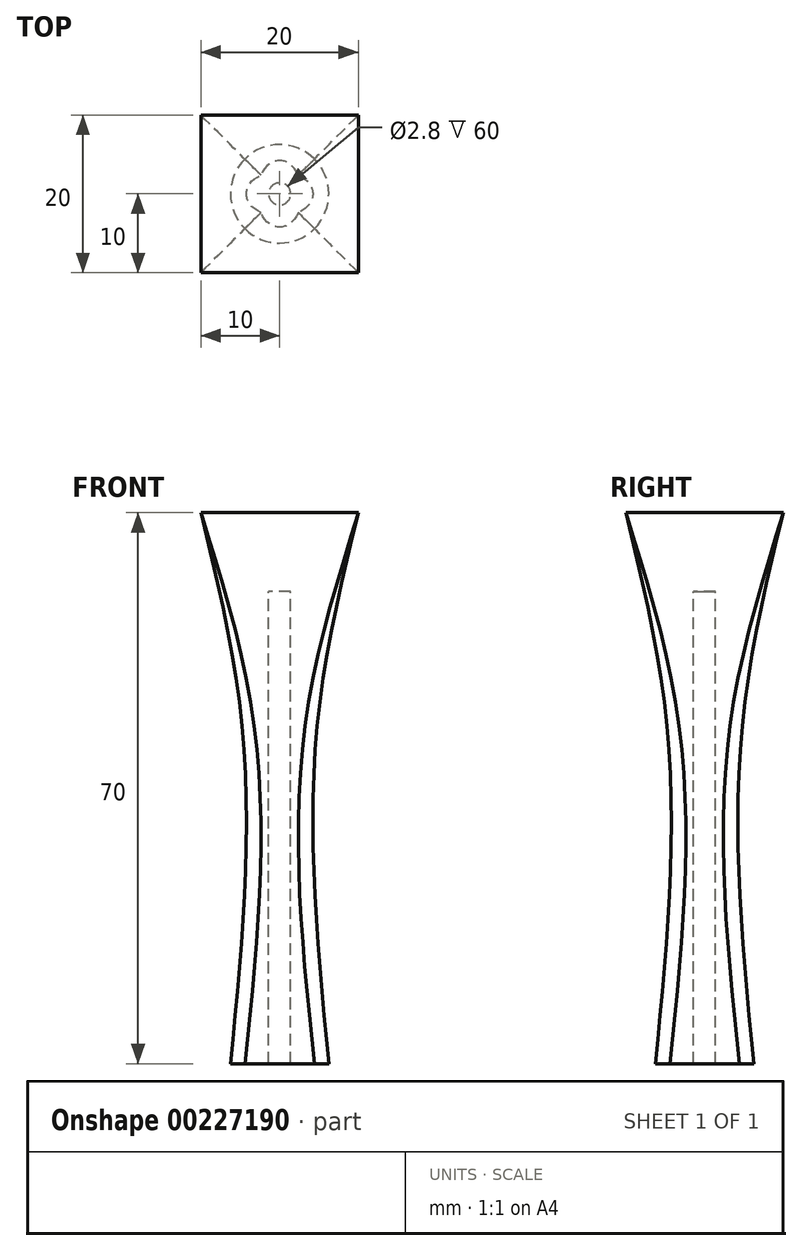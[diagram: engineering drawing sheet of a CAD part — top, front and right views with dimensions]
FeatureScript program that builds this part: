
annotation { "Feature Type Name" : "Feature", "Feature Type Description" : "" }
export const myFeature = defineFeature(function(context is Context, id is Id, definition is map)
    precondition{}
    {
        {
            var Q0;
            Q0=qCreatedBy(makeId("Top.planeOp"),FACE);
            var sketch = newSketch(context, id + "F0", { "sketchPlane" : qUnion([Q0])});
            skLineSegment(sketch, "E0", {"start": v(0, 0) * mm, "end": v(0, 6.25) * mm, "construction": true});
            skArc(sketch, "E1", {"start": v(-4.42, 4.42) * mm, "mid": v(-6.25, 0) * mm, "end": v(-4.42, -4.42) * mm});
            skArc(sketch, "E2", {"start": v(-4.42, -4.42) * mm, "mid": v(0, -6.25) * mm, "end": v(4.42, -4.42) * mm});
            skArc(sketch, "E3", {"start": v(4.42, -4.42) * mm, "mid": v(6.25, 0) * mm, "end": v(4.42, 4.42) * mm});
            skArc(sketch, "E4", {"start": v(4.42, 4.42) * mm, "mid": v(0, 6.25) * mm, "end": v(-4.42, 4.42) * mm});
            skLineSegment(sketch, "E5", {"start": v(-4.42, 4.42) * mm, "end": v(0, 0) * mm, "construction": true});
            skLineSegment(sketch, "E6", {"start": v(0, 0) * mm, "end": v(-4.42, -4.42) * mm, "construction": true});
            skLineSegment(sketch, "E7", {"start": v(0, 0) * mm, "end": v(4.42, -4.42) * mm, "construction": true});
            skLineSegment(sketch, "E8", {"start": v(4.42, 4.42) * mm, "end": v(0, 0) * mm, "construction": true});
            skSolve(sketch);
        }
        {
            var Q0;
            Q0=qCreatedBy(makeId("Top.planeOp"),FACE);
            cPlane(context, id + "F1", {"entities" : qUnion([Q0]), "cplaneType" : CPlaneType.OFFSET, "offset" : 45 * mm, "width" : 150 * mm, "height" : 150 * mm});
        }
        {
            var Q0;
            Q0=qCreatedBy(id+"F1.planeOp",FACE);
            var sketch = newSketch(context, id + "F2", { "sketchPlane" : qUnion([Q0])});
            skCircle(sketch, "E9", {"center": v(0, 0) * mm, "radius": 5 * mm});
            skLineSegment(sketch, "E10", {"start": v(0, 0) * mm, "end": v(0, 5) * mm, "construction": true});
            skLineSegment(sketch, "E11.0", {"start": v(-4.42, 4.42) * mm, "end": v(-3.54, 3.54) * mm, "construction": true});
            skLineSegment(sketch, "E12.0", {"start": v(0, 0) * mm, "end": v(-3.54, -3.54) * mm, "construction": true});
            skLineSegment(sketch, "E13.0", {"start": v(0, 0) * mm, "end": v(3.54, -3.54) * mm, "construction": true});
            skLineSegment(sketch, "E14.0", {"start": v(4.42, 4.42) * mm, "end": v(3.54, 3.54) * mm, "construction": true});
            skLineSegment(sketch, "E15", {"start": v(-3.54, 3.54) * mm, "end": v(0, 0) * mm, "construction": true});
            skLineSegment(sketch, "E16", {"start": v(-3.54, -3.54) * mm, "end": v(-4.42, -4.42) * mm, "construction": true});
            skLineSegment(sketch, "E17", {"start": v(3.54, -3.54) * mm, "end": v(4.42, -4.42) * mm, "construction": true});
            skLineSegment(sketch, "E18", {"start": v(3.54, 3.54) * mm, "end": v(0, 0) * mm, "construction": true});
            skSolve(sketch);
        }
        {
            var Q0;
            Q0=qCreatedBy(id+"F1.planeOp",FACE);
            cPlane(context, id + "F3", {"entities" : qUnion([Q0]), "cplaneType" : CPlaneType.OFFSET, "offset" : 25 * mm, "width" : 150 * mm, "height" : 150 * mm});
        }
        {
            var Q0;
            Q0=qCreatedBy(id+"F3.planeOp",FACE);
            var sketch = newSketch(context, id + "F4", { "sketchPlane" : qUnion([Q0])});
            skLineSegment(sketch, "E19.bottom", {"start": v(-10, 10) * mm, "end": v(10, 10) * mm});
            skLineSegment(sketch, "E19.top", {"start": v(-10, -10) * mm, "end": v(10, -10) * mm});
            skLineSegment(sketch, "E19.left", {"start": v(-10, 10) * mm, "end": v(-10, -10) * mm});
            skLineSegment(sketch, "E19.right", {"start": v(10, 10) * mm, "end": v(10, -10) * mm});
            skPoint(sketch, "E19.middle", {"position": v(0, 0) * mm});
            skSolve(sketch);
        }
        {
            var Q0;
            Q0=makeQuery(id+"F0.imprint","IMPRINT",FACE,{"disambiguationData":[TD([[makeQuery(id+"F0.imprint","IMPRINT",EDGE,{"derivedFrom":sQuery(id+"F0.wireOp",EDGE,"E1")}),1.0]])]});
            var Q1;
            Q1=makeQuery(id+"F2.imprint","IMPRINT",FACE,{"disambiguationData":[TD([[makeQuery(id+"F2.imprint","IMPRINT",EDGE,{"derivedFrom":sQuery(id+"F2.wireOp",EDGE,"E9")}),1.0]])]});
            var Q2;
            Q2=makeQuery(id+"F4.imprint","IMPRINT",FACE,{"disambiguationData":[TD([[makeQuery(id+"F4.imprint","IMPRINT",EDGE,{"derivedFrom":sQuery(id+"F4.wireOp",EDGE,"E19.bottom")}),-1.0]])]});
            loft(context, id + "F5", {"sheetProfilesArray" : [{ "sheetProfileEntities" : qUnion([Q0]) }, { "sheetProfileEntities" : qUnion([Q1]) }, { "sheetProfileEntities" : qUnion([Q2]) }]});
        }
        {
            var Q0;
            Q0=makeQuery(id+"F5.opLoft","CAP_FACE",FACE,{"disambiguationData":[OSD([makeQuery(id+"F4.imprint","IMPRINT",FACE,{"disambiguationData":[TD([[makeQuery(id+"F4.imprint","IMPRINT",EDGE,{"derivedFrom":sQuery(id+"F4.wireOp",EDGE,"E19.bottom")}),-1.0]])]})])],"isStart":true});
            var sketch = newSketch(context, id + "F6", { "sketchPlane" : qUnion([Q0])});
            skCircle(sketch, "E20", {"center": v(0, 0) * mm, "radius": 1.4 * mm});
            skSolve(sketch);
        }
        {
            var Q0;
            Q0=makeQuery(id+"F6.imprint","IMPRINT",FACE,{"disambiguationData":[TD([[makeQuery(id+"F6.imprint","IMPRINT",EDGE,{"derivedFrom":sQuery(id+"F6.wireOp",EDGE,"E20")}),1.0]])]});
            extrude(context, id + "F7", {"entities" : qUnion([Q0]), "operationType" : NewBodyOperationType.REMOVE, "oppositeDirection" : true, "depth" : 200 * mm, "offsetDistance" : 25 * mm});
        }
        {
            var Q0;
            Q0=makeQuery(id+"F5.opLoft","CAP_FACE",FACE,{"disambiguationData":[OSD([makeQuery(id+"F4.imprint","IMPRINT",FACE,{"disambiguationData":[TD([[makeQuery(id+"F4.imprint","IMPRINT",EDGE,{"derivedFrom":sQuery(id+"F4.wireOp",EDGE,"E19.bottom")}),-1.0]])]})])],"isStart":true});
            var sketch = newSketch(context, id + "F8", { "sketchPlane" : qUnion([Q0])});
            skCircle(sketch, "E21.0", {"center": v(0, 0) * mm, "radius": 1.4 * mm});
            skSolve(sketch);
        }
        {
            var Q0;
            Q0=makeQuery(id+"F8.imprint","IMPRINT",FACE,{"disambiguationData":[TD([[makeQuery(id+"F8.imprint","IMPRINT",EDGE,{"derivedFrom":sQuery(id+"F8.wireOp",EDGE,"E21.0")}),1.0]])]});
            extrude(context, id + "F9", {"entities" : qUnion([Q0]), "operationType" : NewBodyOperationType.ADD, "oppositeDirection" : true, "depth" : 10 * mm, "offsetDistance" : 25 * mm});
        }
    });
